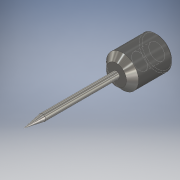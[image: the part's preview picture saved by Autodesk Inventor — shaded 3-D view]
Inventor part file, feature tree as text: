
AUTODESK INVENTOR PART (.ipt)
format: ipt  version: 2016 (Build 200138000, 138)  size: 149,504 bytes
history: native  units: in
note: dims shown in document units (in); Inventor stores cm internally (conversion verified against a paired STEP export)
features: chamfer x2, sketch x2, revolve x1, extrude x1, thread x1, projected_geometry x1
ambient origin geometry x8: Origin, YZ Plane, XZ Plane, XY Plane, X Axis, Y Axis, Z Axis, Center Point
bodies: Solid1 (feature_tree)
feature tree (8):
  revolve  "Revolution1"  [1 undecoded]
  extrude  "Extrusion1"  Depth=0.55in
  chamfer  "Chamfer1"  Angle=90.0deg  [1 undecoded]
  chamfer  "Chamfer2"  Distance=0.1181in
  thread  "Thread2"  [1 undecoded]
  sketch  "Sketch1"  dims[d0=0.1201in d1=0.3in]
  sketch  "Sketch2"  dims[d2=0.025in d3=0.55in d4=90.0deg d5=0.1181in d6=0.128in d7=0.0in d8=0.045in d9=0.125in d10=45.0deg d13=0.5497in d14=0.0687in d15=0.6918in d16=0.9918in d17=0.01in d18=0.125in d19=45.0deg d20=1.0in d21=0.0in]
  projected_geometry  "Projected Loop1"
note: 3 required parameter values undecoded (feature->parameter linkage not recoverable at this tier; creation-order binding heuristic only, values carry confidence <= 0.55)